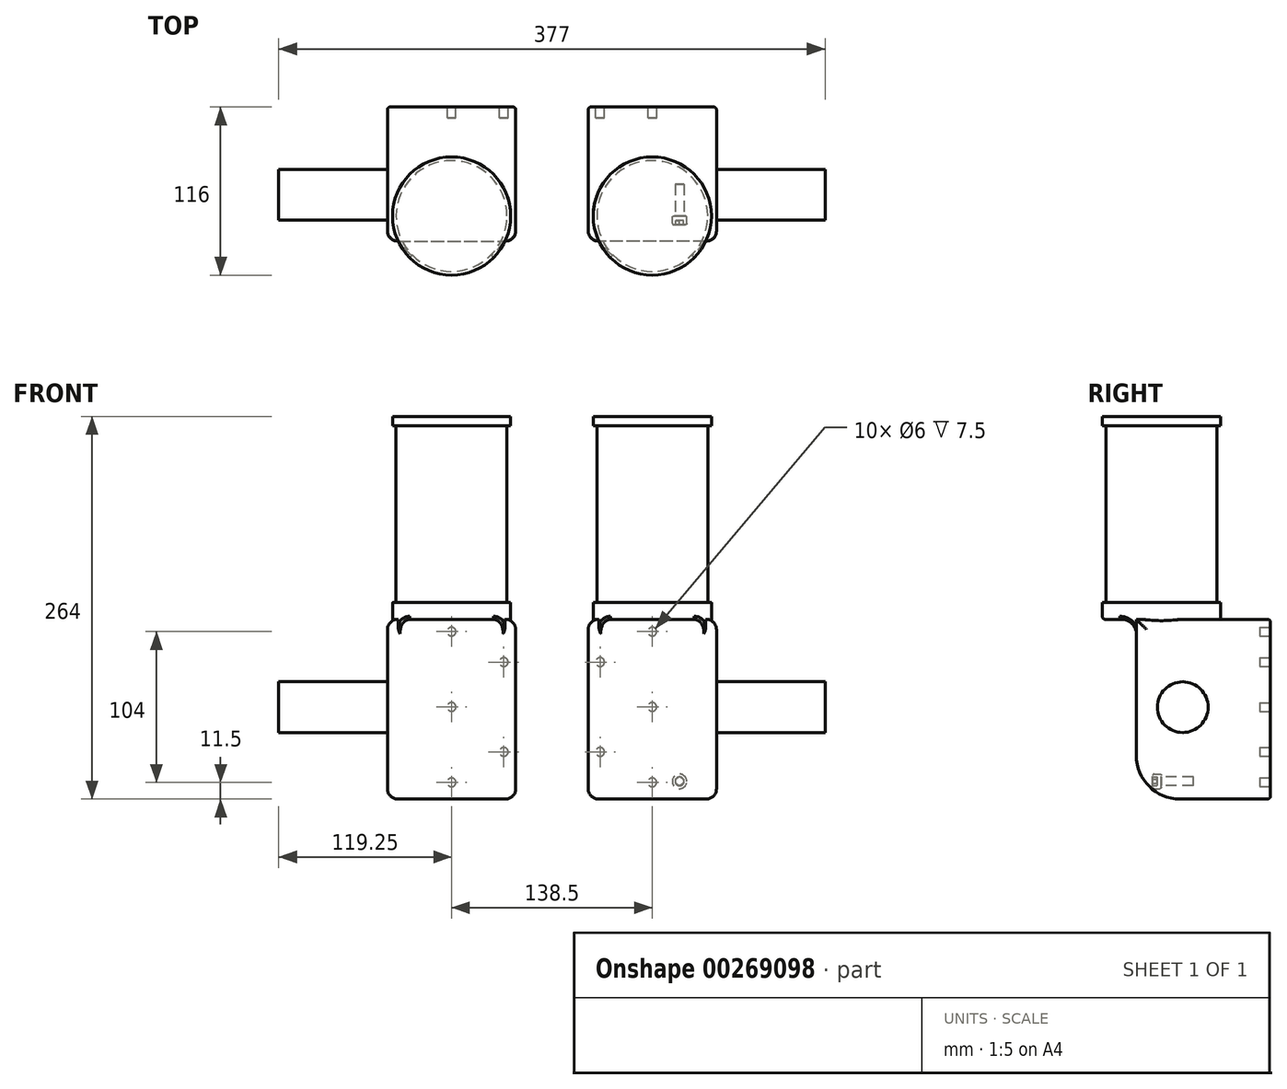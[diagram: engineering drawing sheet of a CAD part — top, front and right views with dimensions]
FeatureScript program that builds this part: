
annotation { "Feature Type Name" : "Feature", "Feature Type Description" : "" }
export const myFeature = defineFeature(function(context is Context, id is Id, definition is map)
    precondition{}
    {
        {
            var Q0;
            Q0=qCreatedBy(makeId("Top.planeOp"),FACE);
            var sketch = newSketch(context, id + "F0", { "sketchPlane" : qUnion([Q0])});
            skCircle(sketch, "E0", {"center": v(0, 0) * mm, "radius": 38.25 * mm});
            skCircle(sketch, "E1", {"center": v(0, 0) * mm, "radius": 40.75 * mm});
            skLineSegment(sketch, "E2", {"start": v(0, 0) * mm, "end": v(0, 40.75) * mm});
            skLineSegment(sketch, "E3", {"start": v(0, 40.75) * mm, "end": v(0, 75.25) * mm});
            skLineSegment(sketch, "E4", {"start": v(0, 75.25) * mm, "end": v(-44.25, 75.25) * mm});
            skLineSegment(sketch, "E5", {"start": v(-44.25, 75.25) * mm, "end": v(-44.25, 0) * mm});
            skLineSegment(sketch, "E6.MirrorCS", {"start": v(44.25, 75.25) * mm, "end": v(44.25, 0) * mm});
            skLineSegment(sketch, "E7.MirrorCS", {"start": v(0, 75.25) * mm, "end": v(44.25, 75.25) * mm});
            skLineSegment(sketch, "E8", {"start": v(-44.25, 75.25) * mm, "end": v(-44.25, -17.25) * mm});
            skLineSegment(sketch, "E9", {"start": v(-44.25, -17.25) * mm, "end": v(44.25, -17.25) * mm});
            skLineSegment(sketch, "E10", {"start": v(44.25, -17.25) * mm, "end": v(44.25, 0) * mm});
            skPoint(sketch, "E11.orphan", {"position": v(44.25, 0) * mm});
            skSolve(sketch);
        }
        {
            var Q0;
            {var subQ4=sQuery(id+"F0.wireOp",EDGE,"E3");Q0=makeQuery(id+"F0.imprint","IMPRINT",FACE,{"disambiguationData":[TD([[makeQuery(id+"F0.imprint","IMPRINT",EDGE,{"derivedFrom":subQ4}),1.0]])]});}
            var Q1;
            {var subQ0=sQuery(id+"F0.wireOp",EDGE,"E3");Q1=makeQuery(id+"F0.imprint","IMPRINT",FACE,{"disambiguationData":[TD([[makeQuery(id+"F0.imprint","IMPRINT",EDGE,{"derivedFrom":subQ0}),-1.0]])]});}
            var Q2;
            {var subQ0=sQuery(id+"F0.wireOp",EDGE,"E0");var subQ1=makeQuery(id+"F0.imprint","INTERSECT",VERTEX,{"derivedFrom":[subQ0,sQuery(id+"F0.wireOp",EDGE,"E2")]});Q2=makeQuery(id+"F0.imprint","IMPRINT",FACE,{"disambiguationData":[TD([[makeQuery(id+"F0.imprint","IMPRINT",EDGE,{"disambiguationData":[TD([[subQ1,-1.0]])],"derivedFrom":subQ0}),1.0]])]});}
            var Q3;
            {var subQ0=sQuery(id+"F0.wireOp",EDGE,"E2");var subQ1=sQuery(id+"F0.wireOp",EDGE,"E0");var subQ2=makeQuery(id+"F0.imprint","INTERSECT",VERTEX,{"derivedFrom":[subQ1,subQ0]});Q3=makeQuery(id+"F0.imprint","IMPRINT",FACE,{"disambiguationData":[TD([[makeQuery(id+"F0.imprint","IMPRINT",EDGE,{"disambiguationData":[TD([[subQ2,-1.0]])],"derivedFrom":subQ1}),-1.0]])]});}
            var Q4;
            {var subQ0=sQuery(id+"F0.wireOp",EDGE,"E2");var subQ1=sQuery(id+"F0.wireOp",EDGE,"E0");var subQ2=makeQuery(id+"F0.imprint","INTERSECT",VERTEX,{"derivedFrom":[subQ1,subQ0]});Q4=makeQuery(id+"F0.imprint","IMPRINT",FACE,{"disambiguationData":[TD([[makeQuery(id+"F0.imprint","IMPRINT",EDGE,{"disambiguationData":[TD([[subQ2,1.0]])],"derivedFrom":subQ1}),-1.0]])]});}
            extrude(context, id + "F1", {"entities" : qUnion([Q0, Q1, Q2, Q3, Q4]), "oppositeDirection" : true, "depth" : 124 * mm});
        }
        {
            var Q0;
            {var subQ0=sQuery(id+"F0.wireOp",EDGE,"E2");var subQ1=sQuery(id+"F0.wireOp",EDGE,"E0");var subQ2=makeQuery(id+"F0.imprint","INTERSECT",VERTEX,{"derivedFrom":[subQ1,subQ0]});Q0=makeQuery(id+"F0.imprint","IMPRINT",FACE,{"disambiguationData":[TD([[makeQuery(id+"F0.imprint","IMPRINT",EDGE,{"disambiguationData":[TD([[subQ2,-1.0]])],"derivedFrom":subQ1}),-1.0]])]});}
            var Q1;
            {var subQ0=sQuery(id+"F0.wireOp",EDGE,"E2");var subQ1=sQuery(id+"F0.wireOp",EDGE,"E0");var subQ2=makeQuery(id+"F0.imprint","INTERSECT",VERTEX,{"derivedFrom":[subQ1,subQ0]});Q1=makeQuery(id+"F0.imprint","IMPRINT",FACE,{"disambiguationData":[TD([[makeQuery(id+"F0.imprint","IMPRINT",EDGE,{"disambiguationData":[TD([[subQ2,1.0]])],"derivedFrom":subQ1}),-1.0]])]});}
            var Q2;
            {var subQ0=sQuery(id+"F0.wireOp",EDGE,"E9");var subQ1=sQuery(id+"F0.wireOp",EDGE,"E0");var subQ2=makeQuery(id+"F0.imprint","INTERSECT",VERTEX,{"disambiguationData":[OD(0.0)],"derivedFrom":[subQ1,subQ0]});Q2=makeQuery(id+"F0.imprint","IMPRINT",FACE,{"disambiguationData":[TD([[makeQuery(id+"F0.imprint","IMPRINT",EDGE,{"disambiguationData":[TD([[subQ2,-1.0]])],"derivedFrom":subQ1}),-1.0]])]});}
            extrude(context, id + "F2", {"entities" : qUnion([Q0, Q1, Q2]), "operationType" : NewBodyOperationType.ADD, "depth" : 11.5 * mm});
        }
        {
            var Q0;
            {var subQ0=sQuery(id+"F0.wireOp",EDGE,"E0");var subQ1=makeQuery(id+"F0.imprint","INTERSECT",VERTEX,{"derivedFrom":[subQ0,sQuery(id+"F0.wireOp",EDGE,"E2")]});Q0=makeQuery(id+"F0.imprint","IMPRINT",FACE,{"disambiguationData":[TD([[makeQuery(id+"F0.imprint","IMPRINT",EDGE,{"disambiguationData":[TD([[subQ1,-1.0]])],"derivedFrom":subQ0}),1.0]])]});}
            var Q1;
            {var subQ0=sQuery(id+"F0.wireOp",EDGE,"E9");var subQ1=sQuery(id+"F0.wireOp",EDGE,"E0");var subQ2=makeQuery(id+"F0.imprint","INTERSECT",VERTEX,{"disambiguationData":[OD(0.0)],"derivedFrom":[subQ1,subQ0]});Q1=makeQuery(id+"F0.imprint","IMPRINT",FACE,{"disambiguationData":[TD([[makeQuery(id+"F0.imprint","IMPRINT",EDGE,{"disambiguationData":[TD([[subQ2,-1.0]])],"derivedFrom":subQ1}),1.0]])]});}
            extrude(context, id + "F3", {"entities" : qUnion([Q0, Q1]), "operationType" : NewBodyOperationType.ADD, "depth" : 133.5 * mm});
        }
        {
            var Q0;
            Q0=makeQuery(id+"F3.opExtrude","CAP_FACE",FACE,{"disambiguationData":[OSD([sQuery(id+"F0.wireOp",EDGE,"E0")])],"isStart":false});
            var sketch = newSketch(context, id + "F4", { "sketchPlane" : qUnion([Q0])});
            skCircle(sketch, "E12", {"center": v(0, 0) * mm, "radius": 40.75 * mm});
            skSolve(sketch);
        }
        {
            var Q0;
            Q0=qSketchRegion(id+"F4",true);
            extrude(context, id + "F5", {"entities" : qUnion([Q0]), "operationType" : NewBodyOperationType.ADD, "depth" : 6.5 * mm});
        }
        {
            var Q0;
            Q0=makeQuery(id+"F1.opExtrude","CAP_EDGE",EDGE,{"disambiguationData":[OSD([sQuery(id+"F0.wireOp",EDGE,"E9")])],"isStart":false});
            fillet(context, id + "F6", {"entities" : qUnion([Q0]), "radius" : 30 * mm, "tangentPropagation" : true, "allowEdgeOverflow" : false});
        }
        {
            var Q0;
            Q0=makeQuery(id+"F1.opExtrude","CAP_EDGE",EDGE,{"disambiguationData":[OSD([sQuery(id+"F0.wireOp",EDGE,"E8")])],"isStart":true});
            var Q1;
            Q1=makeQuery(id+"F1.opExtrude","CAP_EDGE",EDGE,{"disambiguationData":[OSD([sQuery(id+"F0.wireOp",EDGE,"E8")])],"isStart":false});
            var Q2;
            Q2=makeQuery(id+"F1.opExtrude","CAP_EDGE",EDGE,{"disambiguationData":[OSD([sQuery(id+"F0.wireOp",EDGE,"E6.MirrorCS"),sQuery(id+"F0.wireOp",EDGE,"E10")])],"isStart":false});
            var Q3;
            Q3=makeQuery(id+"F1.opExtrude","CAP_EDGE",EDGE,{"disambiguationData":[OSD([sQuery(id+"F0.wireOp",EDGE,"E6.MirrorCS"),sQuery(id+"F0.wireOp",EDGE,"E10")])],"isStart":true});
            fillet(context, id + "F7", {"entities" : qUnion([Q0, Q1, Q2, Q3]), "radius" : 7 * mm, "tangentPropagation" : true, "allowEdgeOverflow" : false});
        }
        {
            var Q0;
            Q0=makeQuery(id+"F1.opExtrude","SWEPT_FACE",FACE,{"disambiguationData":[OSD([sQuery(id+"F0.wireOp",EDGE,"E4"),sQuery(id+"F0.wireOp",EDGE,"E7.MirrorCS")])]});
            var sketch = newSketch(context, id + "F8", { "sketchPlane" : qUnion([Q0])});
            skLineSegment(sketch, "E13", {"start": v(0, 0) * mm, "end": v(0, -8.5) * mm});
            skLineSegment(sketch, "E14", {"start": v(0, -8.5) * mm, "end": v(0, -60.5) * mm});
            skLineSegment(sketch, "E15", {"start": v(0, -60.5) * mm, "end": v(0, -112.5) * mm});
            skCircle(sketch, "E16", {"center": v(0, -8.5) * mm, "radius": 3 * mm});
            skCircle(sketch, "E17", {"center": v(0, -60.5) * mm, "radius": 3 * mm});
            skCircle(sketch, "E18", {"center": v(0, -112.5) * mm, "radius": 3 * mm});
            skLineSegment(sketch, "E19", {"start": v(0, -112.5) * mm, "end": v(-36, -112.5) * mm});
            skLineSegment(sketch, "E20", {"start": v(-36, -112.5) * mm, "end": v(-36, -91.5) * mm});
            skLineSegment(sketch, "E21", {"start": v(-36, -91.5) * mm, "end": v(-36, -29.5) * mm});
            skCircle(sketch, "E22", {"center": v(-36, -29.5) * mm, "radius": 3 * mm});
            skCircle(sketch, "E23", {"center": v(-36, -91.5) * mm, "radius": 3 * mm});
            skLineSegment(sketch, "E24", {"start": v(0, -60.5) * mm, "end": v(44.25, -60.5) * mm});
            skSolve(sketch);
        }
        {
            var Q0;
            {var subQ0=sQuery(id+"F0.wireOp",EDGE,"E9");var subQ1=makeQuery(id+"F1.opExtrude","SWEPT_FACE",FACE,{"disambiguationData":[OSD([subQ0])]});var subQ2=sQuery(id+"F0.wireOp",EDGE,"E0");var subQ3=makeQuery(id+"F2.opExtrude","CAP_FACE",FACE,{"disambiguationData":[OSD([subQ2,sQuery(id+"F0.wireOp",EDGE,"E1")])],"isStart":true});var subQ4=makeQuery(id+"F1.opExtrude","CAP_EDGE",EDGE,{"disambiguationData":[OSD([subQ0])],"isStart":true});var subQ5=makeQuery(id+"F1.opExtrude","CAP_FACE",FACE,{"disambiguationData":[OSD([sQuery(id+"F0.wireOp",EDGE,"E4"),sQuery(id+"F0.wireOp",EDGE,"E6.MirrorCS"),sQuery(id+"F0.wireOp",EDGE,"E7.MirrorCS"),sQuery(id+"F0.wireOp",EDGE,"E8"),subQ0,sQuery(id+"F0.wireOp",EDGE,"E10")])],"isStart":true});Q0=makeQuery(id+"F3.boolean.opBoolean","MERGE",EDGE,{"derivedFrom":[makeQuery(id+"F2.boolean.opBoolean","SPLIT",EDGE,{"disambiguationData":[topologyDisambiguationEdgeConnected([subQ5,subQ1]),TD([makeQuery(id+"F2.opExtrude","SWEPT_FACE",FACE,{"disambiguationData":[OSD([subQ2])]})])],"derivedFrom":subQ4}),makeQuery(id+"F2.boolean.opBoolean","SPLIT",EDGE,{"disambiguationData":[topologyDisambiguationEdgeConnected([subQ1,subQ3]),OD(0.0)],"derivedFrom":subQ4}),makeQuery(id+"F2.boolean.opBoolean","SPLIT",EDGE,{"disambiguationData":[topologyDisambiguationEdgeConnected([subQ1,subQ3]),OD(1.0)],"derivedFrom":subQ4})]});}
            fillet(context, id + "F9", {"entities" : qUnion([Q0]), "radius" : 10 * mm, "tangentPropagation" : true, "allowEdgeOverflow" : false});
        }
        {
            var Q0;
            Q0=qCreatedBy(makeId("Front.planeOp"),FACE);
            var sketch = newSketch(context, id + "F10", { "sketchPlane" : qUnion([Q0])});
            skCircle(sketch, "E25", {"center": v(157.3, -111.85) * mm, "radius": 5 * mm});
            skCircle(sketch, "E26", {"center": v(157.3, -111.85) * mm, "radius": 3 * mm});
            skLineSegment(sketch, "E27", {"start": v(157.3, -108.85) * mm, "end": v(154.65, -110.45) * mm});
            skLineSegment(sketch, "E28", {"start": v(159.95, -110.45) * mm, "end": v(157.3, -108.85) * mm});
            skLineSegment(sketch, "E29", {"start": v(159.95, -110.45) * mm, "end": v(159.95, -113.17) * mm});
            skLineSegment(sketch, "E30", {"start": v(159.95, -113.17) * mm, "end": v(157.3, -114.85) * mm});
            skLineSegment(sketch, "E31", {"start": v(154.6, -113.17) * mm, "end": v(154.65, -110.45) * mm});
            skLineSegment(sketch, "E32", {"start": v(154.6, -113.17) * mm, "end": v(157.3, -114.85) * mm});
            skSolve(sketch);
        }
        {
            var Q0;
            Q0=makeQuery(id+"F10.imprint","IMPRINT",FACE,{"disambiguationData":[TD([[makeQuery(id+"F10.imprint","IMPRINT",EDGE,{"derivedFrom":sQuery(id+"F10.wireOp",EDGE,"E25")}),1.0]])]});
            extrude(context, id + "F11", {"entities" : qUnion([Q0]), "depth" : 6 * mm});
        }
        {
            var Q0;
            Q0=makeQuery(id+"F10.imprint","IMPRINT",FACE,{"disambiguationData":[TD([[makeQuery(id+"F10.imprint","IMPRINT",EDGE,{"derivedFrom":sQuery(id+"F10.wireOp",EDGE,"E27")}),1.0]])]});
            var Q1;
            {var subQ0=sQuery(id+"F10.wireOp",EDGE,"E29");Q1=makeQuery(id+"F10.imprint","IMPRINT",FACE,{"disambiguationData":[TD([[makeQuery(id+"F10.imprint","IMPRINT",EDGE,{"derivedFrom":subQ0}),1.0]])]});}
            var Q2;
            {var subQ0=sQuery(id+"F10.wireOp",EDGE,"E32");Q2=makeQuery(id+"F10.imprint","IMPRINT",FACE,{"disambiguationData":[TD([[makeQuery(id+"F10.imprint","IMPRINT",EDGE,{"derivedFrom":subQ0}),-1.0]])]});}
            var Q3;
            {var subQ0=sQuery(id+"F10.wireOp",EDGE,"E31");Q3=makeQuery(id+"F10.imprint","IMPRINT",FACE,{"disambiguationData":[TD([[makeQuery(id+"F10.imprint","IMPRINT",EDGE,{"derivedFrom":subQ0}),1.0]])]});}
            var Q4;
            {var subQ0=sQuery(id+"F10.wireOp",EDGE,"E27");Q4=makeQuery(id+"F10.imprint","IMPRINT",FACE,{"disambiguationData":[TD([[makeQuery(id+"F10.imprint","IMPRINT",EDGE,{"derivedFrom":subQ0}),-1.0]])]});}
            var Q5;
            {var subQ0=sQuery(id+"F10.wireOp",EDGE,"E28");Q5=makeQuery(id+"F10.imprint","IMPRINT",FACE,{"disambiguationData":[TD([[makeQuery(id+"F10.imprint","IMPRINT",EDGE,{"derivedFrom":subQ0}),-1.0]])]});}
            extrude(context, id + "F12", {"entities" : qUnion([Q0, Q1, Q2, Q3, Q4, Q5]), "operationType" : NewBodyOperationType.ADD, "endBound" : BoundingType.SYMMETRIC, "oppositeDirection" : true, "depth" : 4 * mm});
        }
        {
            var Q0;
            {var subQ0=sQuery(id+"F10.wireOp",EDGE,"E29");Q0=makeQuery(id+"F10.imprint","IMPRINT",FACE,{"disambiguationData":[TD([[makeQuery(id+"F10.imprint","IMPRINT",EDGE,{"derivedFrom":subQ0}),1.0]])]});}
            var Q1;
            {var subQ0=sQuery(id+"F10.wireOp",EDGE,"E28");Q1=makeQuery(id+"F10.imprint","IMPRINT",FACE,{"disambiguationData":[TD([[makeQuery(id+"F10.imprint","IMPRINT",EDGE,{"derivedFrom":subQ0}),-1.0]])]});}
            var Q2;
            {var subQ0=sQuery(id+"F10.wireOp",EDGE,"E27");Q2=makeQuery(id+"F10.imprint","IMPRINT",FACE,{"disambiguationData":[TD([[makeQuery(id+"F10.imprint","IMPRINT",EDGE,{"derivedFrom":subQ0}),-1.0]])]});}
            var Q3;
            {var subQ0=sQuery(id+"F10.wireOp",EDGE,"E31");Q3=makeQuery(id+"F10.imprint","IMPRINT",FACE,{"disambiguationData":[TD([[makeQuery(id+"F10.imprint","IMPRINT",EDGE,{"derivedFrom":subQ0}),1.0]])]});}
            var Q4;
            {var subQ0=sQuery(id+"F10.wireOp",EDGE,"E32");Q4=makeQuery(id+"F10.imprint","IMPRINT",FACE,{"disambiguationData":[TD([[makeQuery(id+"F10.imprint","IMPRINT",EDGE,{"derivedFrom":subQ0}),-1.0]])]});}
            var Q5;
            Q5=makeQuery(id+"F11.opExtrude","CAP_FACE",FACE,{"disambiguationData":[OSD([sQuery(id+"F10.wireOp",EDGE,"E25"),sQuery(id+"F10.wireOp",EDGE,"E26")])],"isStart":false});
            extrude(context, id + "F13", {"entities" : qUnion([Q0, Q1, Q2, Q3, Q4]), "operationType" : NewBodyOperationType.ADD, "endBound" : BoundingType.UP_TO_SURFACE, "endBoundEntityFace" : qUnion([Q5]), "depth" : 25 * mm});
        }
        {
            var Q0;
            Q0=makeQuery(id+"F10.imprint","IMPRINT",FACE,{"disambiguationData":[TD([[makeQuery(id+"F10.imprint","IMPRINT",EDGE,{"derivedFrom":sQuery(id+"F10.wireOp",EDGE,"E27")}),1.0]])]});
            extrude(context, id + "F14", {"entities" : qUnion([Q0]), "operationType" : NewBodyOperationType.ADD, "depth" : 3 * mm});
        }
        {
            var Q0;
            Q0=makeQuery(id+"F12.opExtrude","CAP_FACE",FACE,{"disambiguationData":[OSD([sQuery(id+"F10.wireOp",EDGE,"E26")])],"isStart":false});
            extrude(context, id + "F15", {"entities" : qUnion([Q0]), "operationType" : NewBodyOperationType.ADD, "depth" : 20 * mm});
        }
        {
            var Q0;
            Q0=makeQuery(id+"F11.opExtrude","CAP_EDGE",EDGE,{"disambiguationData":[OSD([sQuery(id+"F10.wireOp",EDGE,"E25")])],"isStart":false});
            var Q1;
            Q1=makeQuery(id+"F11.opExtrude","CAP_EDGE",EDGE,{"disambiguationData":[OSD([sQuery(id+"F10.wireOp",EDGE,"E25")])],"isStart":true});
            fillet(context, id + "F16", {"entities" : qUnion([Q0, Q1]), "radius" : 1 * mm, "tangentPropagation" : true, "allowEdgeOverflow" : false});
        }
        {
            var Q0;
            Q0=makeQuery(id+"F8.imprint","IMPRINT",FACE,{"disambiguationData":[TD([[makeQuery(id+"F8.imprint","IMPRINT",EDGE,{"derivedFrom":sQuery(id+"F8.wireOp",EDGE,"E18")}),1.0]])]});
            var Q1;
            {var subQ0=sQuery(id+"F8.wireOp",EDGE,"E15");var subQ1=sQuery(id+"F8.wireOp",EDGE,"E14");var subQ2=makeQuery(id+"F8.imprint","INTERSECT",VERTEX,{"derivedFrom":[subQ1,subQ0]});Q1=makeQuery(id+"F8.imprint","IMPRINT",FACE,{"disambiguationData":[TD([[makeQuery(id+"F8.imprint","IMPRINT",EDGE,{"disambiguationData":[TD([[subQ2,1.0]])],"derivedFrom":subQ1}),1.0]])]});}
            var Q2;
            {var subQ0=sQuery(id+"F8.wireOp",EDGE,"E15");var subQ1=sQuery(id+"F8.wireOp",EDGE,"E14");var subQ2=makeQuery(id+"F8.imprint","INTERSECT",VERTEX,{"derivedFrom":[subQ1,subQ0]});Q2=makeQuery(id+"F8.imprint","IMPRINT",FACE,{"disambiguationData":[TD([[makeQuery(id+"F8.imprint","IMPRINT",EDGE,{"disambiguationData":[TD([[subQ2,1.0]])],"derivedFrom":subQ1}),-1.0]])]});}
            var Q3;
            {var subQ0=sQuery(id+"F8.wireOp",EDGE,"E14");var subQ1=sQuery(id+"F8.wireOp",EDGE,"E13");var subQ2=makeQuery(id+"F8.imprint","INTERSECT",VERTEX,{"derivedFrom":[subQ1,subQ0]});Q3=makeQuery(id+"F8.imprint","IMPRINT",FACE,{"disambiguationData":[TD([[makeQuery(id+"F8.imprint","IMPRINT",EDGE,{"disambiguationData":[TD([[subQ2,1.0]])],"derivedFrom":subQ1}),1.0]])]});}
            var Q4;
            {var subQ0=sQuery(id+"F8.wireOp",EDGE,"E14");var subQ1=sQuery(id+"F8.wireOp",EDGE,"E13");var subQ2=makeQuery(id+"F8.imprint","INTERSECT",VERTEX,{"derivedFrom":[subQ1,subQ0]});Q4=makeQuery(id+"F8.imprint","IMPRINT",FACE,{"disambiguationData":[TD([[makeQuery(id+"F8.imprint","IMPRINT",EDGE,{"disambiguationData":[TD([[subQ2,1.0]])],"derivedFrom":subQ1}),-1.0]])]});}
            var Q5;
            {var subQ0=sQuery(id+"F8.wireOp",EDGE,"E21");var subQ1=sQuery(id+"F8.wireOp",EDGE,"E20");var subQ2=makeQuery(id+"F8.imprint","INTERSECT",VERTEX,{"derivedFrom":[subQ1,subQ0]});Q5=makeQuery(id+"F8.imprint","IMPRINT",FACE,{"disambiguationData":[TD([[makeQuery(id+"F8.imprint","IMPRINT",EDGE,{"disambiguationData":[TD([[subQ2,1.0]])],"derivedFrom":subQ1}),-1.0]])]});}
            var Q6;
            {var subQ0=sQuery(id+"F8.wireOp",EDGE,"E21");var subQ1=sQuery(id+"F8.wireOp",EDGE,"E20");var subQ2=makeQuery(id+"F8.imprint","INTERSECT",VERTEX,{"derivedFrom":[subQ1,subQ0]});Q6=makeQuery(id+"F8.imprint","IMPRINT",FACE,{"disambiguationData":[TD([[makeQuery(id+"F8.imprint","IMPRINT",EDGE,{"disambiguationData":[TD([[subQ2,1.0]])],"derivedFrom":subQ1}),1.0]])]});}
            var Q7;
            Q7=makeQuery(id+"F8.imprint","IMPRINT",FACE,{"disambiguationData":[TD([[makeQuery(id+"F8.imprint","IMPRINT",EDGE,{"derivedFrom":sQuery(id+"F8.wireOp",EDGE,"E22")}),1.0]])]});
            var Q8;
            {var subQ1=sQuery(id+"F8.wireOp",EDGE,"E15");var subQ3=sQuery(id+"F8.wireOp",EDGE,"E17");var subQ4=makeQuery(id+"F8.imprint","INTERSECT",VERTEX,{"derivedFrom":[subQ1,subQ3]});Q8=makeQuery(id+"F8.imprint","IMPRINT",FACE,{"disambiguationData":[TD([[makeQuery(id+"F8.imprint","IMPRINT",EDGE,{"disambiguationData":[TD([[subQ4,-1.0]])],"derivedFrom":subQ3}),1.0]])]});}
            extrude(context, id + "F17", {"entities" : qUnion([Q0, Q1, Q2, Q3, Q4, Q5, Q6, Q7, Q8]), "operationType" : NewBodyOperationType.REMOVE, "oppositeDirection" : true, "depth" : 7.5 * mm});
        }
        {
            var Q0;
            Q0=makeQuery(id+"F1.opExtrude","SWEPT_FACE",FACE,{"disambiguationData":[OSD([sQuery(id+"F0.wireOp",EDGE,"E8")])]});
            var sketch = newSketch(context, id + "F18", { "sketchPlane" : qUnion([Q0])});
            skLineSegment(sketch, "E33", {"start": v(-75.25, -60.63) * mm, "end": v(-29.25, -60.63) * mm});
            skLineSegment(sketch, "E34", {"start": v(-75.25, -60.63) * mm, "end": v(2.75, -60.63) * mm});
            skCircle(sketch, "E35", {"center": v(-14.75, -60.63) * mm, "radius": 17.5 * mm});
            skSolve(sketch);
        }
        {
            var Q0;
            {var subQ0=sQuery(id+"F18.wireOp",EDGE,"E34");var subQ1=makeQuery(id+"F18.imprint","IMPRINT",VERTEX,{"derivedFrom":subQ0});Q0=makeQuery(id+"F18.imprint","IMPRINT",FACE,{"disambiguationData":[TD([[makeQuery(id+"F18.imprint","IMPRINT",EDGE,{"disambiguationData":[TD([[subQ1,1.0]])],"derivedFrom":subQ0}),-1.0]])]});}
            var Q1;
            {var subQ0=sQuery(id+"F18.wireOp",EDGE,"E34");var subQ1=makeQuery(id+"F18.imprint","IMPRINT",VERTEX,{"derivedFrom":subQ0});Q1=makeQuery(id+"F18.imprint","IMPRINT",FACE,{"disambiguationData":[TD([[makeQuery(id+"F18.imprint","IMPRINT",EDGE,{"disambiguationData":[TD([[subQ1,1.0]])],"derivedFrom":subQ0}),1.0]])]});}
            extrude(context, id + "F19", {"entities" : qUnion([Q0, Q1]), "operationType" : NewBodyOperationType.ADD, "depth" : 75 * mm});
        }
        {
            var Q0;
            Q0=makeQuery(id+"F1.opExtrude","SWEPT_BODY",BODY,{"disambiguationData":[OSD([sQuery(id+"F0.wireOp",EDGE,"E4"),sQuery(id+"F0.wireOp",EDGE,"E6.MirrorCS"),sQuery(id+"F0.wireOp",EDGE,"E7.MirrorCS"),sQuery(id+"F0.wireOp",EDGE,"E8"),sQuery(id+"F0.wireOp",EDGE,"E9"),sQuery(id+"F0.wireOp",EDGE,"E10")])]});
            var Q1;
            Q1=makeQuery(id+"F1.opExtrude","SWEPT_FACE",FACE,{"disambiguationData":[OSD([sQuery(id+"F0.wireOp",EDGE,"E6.MirrorCS"),sQuery(id+"F0.wireOp",EDGE,"E10")])]});
            mirror(context, id + "F20", {"entities" : qUnion([Q0]), "mirrorPlane" : qUnion([Q1])});
        }
        {
            var Q0;
            Q0=makeQuery(id+"F20.opPattern","COPY",BODY,{"derivedFrom":makeQuery(id+"F1.opExtrude","SWEPT_BODY",BODY,{"disambiguationData":[OSD([sQuery(id+"F0.wireOp",EDGE,"E4"),sQuery(id+"F0.wireOp",EDGE,"E6.MirrorCS"),sQuery(id+"F0.wireOp",EDGE,"E7.MirrorCS"),sQuery(id+"F0.wireOp",EDGE,"E8"),sQuery(id+"F0.wireOp",EDGE,"E9"),sQuery(id+"F0.wireOp",EDGE,"E10")])]}),"instanceName":"1"});
            var Q1;
            Q1=makeQuery(id+"F20.opPattern","COPY",EDGE,{"derivedFrom":makeQuery(id+"F19.opExtrude","CAP_EDGE",EDGE,{"disambiguationData":[OSD([sQuery(id+"F18.wireOp",EDGE,"E35")])],"isStart":false}),"instanceName":"1"});
            transform(context, id + "F21", {"entities" : qUnion([Q0]), "transformType" : TransformType.TRANSLATION_3D, "dx" : 50 * mm, "dy" : 0 * mm, "dz" : 0 * mm, "makeCopy" : false});
        }
        {
            var Q0;
            Q0=makeQuery(id+"F1.opExtrude","CAP_EDGE",EDGE,{"disambiguationData":[OSD([sQuery(id+"F0.wireOp",EDGE,"E4"),sQuery(id+"F0.wireOp",EDGE,"E7.MirrorCS")])],"isStart":true});
            var Q1;
            Q1=makeQuery(id+"F20.opPattern","COPY",EDGE,{"derivedFrom":makeQuery(id+"F1.opExtrude","CAP_EDGE",EDGE,{"disambiguationData":[OSD([sQuery(id+"F0.wireOp",EDGE,"E4"),sQuery(id+"F0.wireOp",EDGE,"E7.MirrorCS")])],"isStart":true}),"instanceName":"1"});
            fillet(context, id + "F22", {"entities" : qUnion([Q0, Q1]), "radius" : 2 * mm, "tangentPropagation" : true, "allowEdgeOverflow" : false});
        }
        {
            var Q0;
            {var subQ0=sQuery(id+"F0.wireOp",EDGE,"E1");Q0=makeQuery(id+"F20.opPattern","COPY",EDGE,{"derivedFrom":makeQuery(id+"F2.boolean.opBoolean","SPLIT",EDGE,{"disambiguationData":[topologyDisambiguationEdgeConnected([makeQuery(id+"F2.opExtrude","CAP_FACE",FACE,{"disambiguationData":[OSD([sQuery(id+"F0.wireOp",EDGE,"E0"),subQ0])],"isStart":true})])],"derivedFrom":makeQuery(id+"F2.opExtrude","CAP_EDGE",EDGE,{"disambiguationData":[OSD([subQ0])],"isStart":true})}),"instanceName":"1"});}
            var Q1;
            {var subQ0=sQuery(id+"F0.wireOp",EDGE,"E1");Q1=makeQuery(id+"F2.boolean.opBoolean","SPLIT",EDGE,{"disambiguationData":[topologyDisambiguationEdgeConnected([makeQuery(id+"F2.opExtrude","CAP_FACE",FACE,{"disambiguationData":[OSD([sQuery(id+"F0.wireOp",EDGE,"E0"),subQ0])],"isStart":true})])],"derivedFrom":makeQuery(id+"F2.opExtrude","CAP_EDGE",EDGE,{"disambiguationData":[OSD([subQ0])],"isStart":true})});}
            fillet(context, id + "F23", {"entities" : qUnion([Q0, Q1]), "radius" : 2 * mm, "tangentPropagation" : true, "allowEdgeOverflow" : false});
        }
    });
